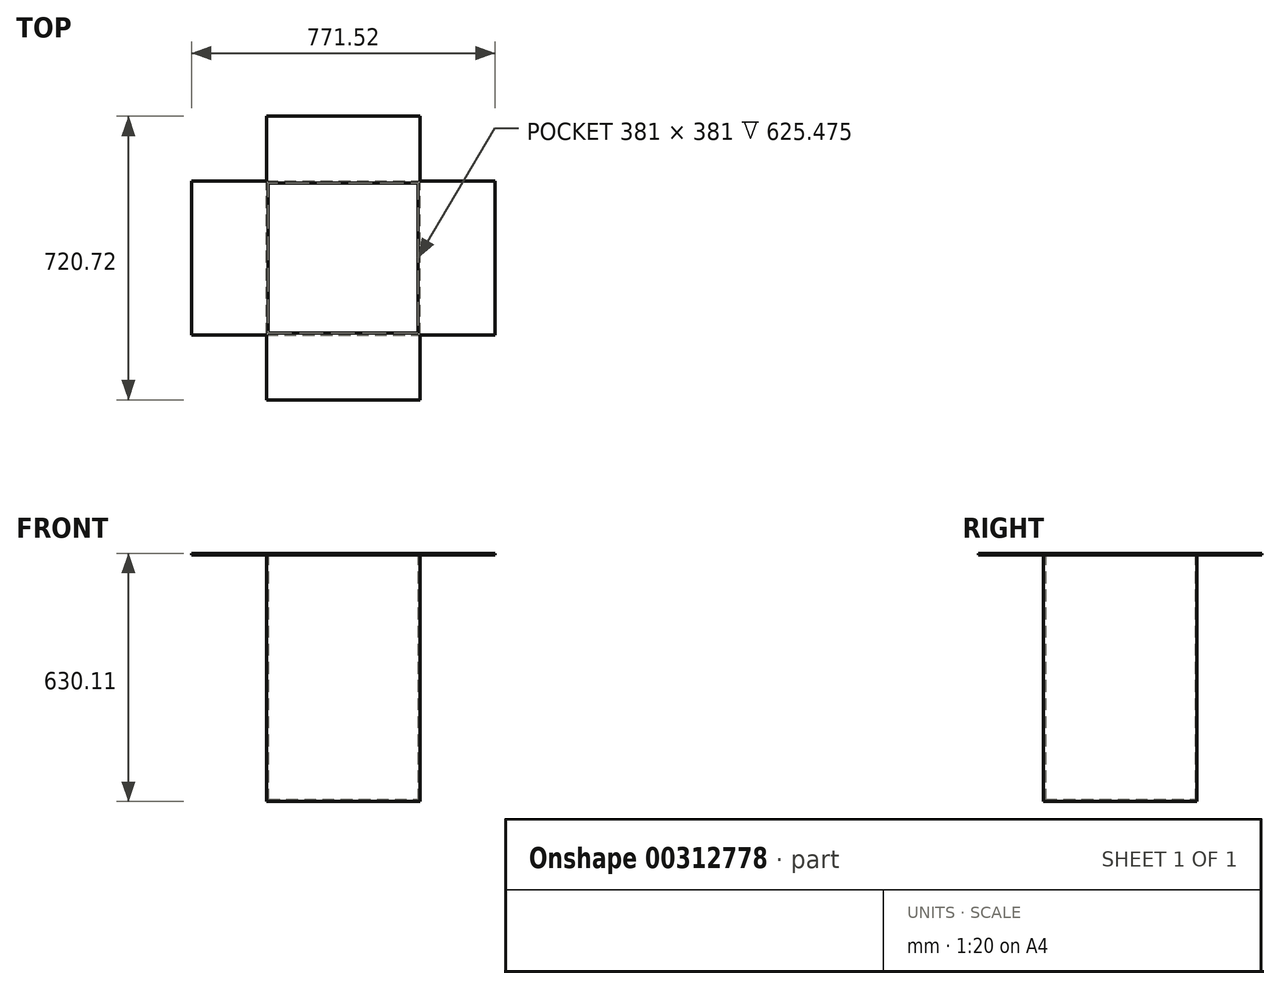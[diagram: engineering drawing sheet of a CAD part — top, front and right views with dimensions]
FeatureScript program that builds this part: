
annotation { "Feature Type Name" : "Feature", "Feature Type Description" : "" }
export const myFeature = defineFeature(function(context is Context, id is Id, definition is map)
    precondition{}
    {
        {
            var Q0;
            Q0=qCreatedBy(makeId("Top.planeOp"),FACE);
            var sketch = newSketch(context, id + "F0", { "sketchPlane" : qUnion([Q0])});
            skLineSegment(sketch, "E0.bottom", {"start": v(0, 0) * mm, "end": v(390.53, 0) * mm});
            skLineSegment(sketch, "E0.top", {"start": v(0, 390.53) * mm, "end": v(390.53, 390.53) * mm});
            skLineSegment(sketch, "E0.left", {"start": v(0, 0) * mm, "end": v(0, 390.53) * mm});
            skLineSegment(sketch, "E0.right", {"start": v(390.53, 0) * mm, "end": v(390.53, 390.53) * mm});
            skLineSegment(sketch, "E1.0", {"start": v(4.76, 4.76) * mm, "end": v(4.76, 385.76) * mm});
            skLineSegment(sketch, "E1.1", {"start": v(4.76, 4.76) * mm, "end": v(385.76, 4.76) * mm});
            skLineSegment(sketch, "E1.2", {"start": v(385.76, 4.76) * mm, "end": v(385.76, 385.76) * mm});
            skLineSegment(sketch, "E1.3", {"start": v(4.76, 385.76) * mm, "end": v(385.76, 385.76) * mm});
            skSolve(sketch);
        }
        {
            var Q0;
            Q0 = qSketchRegion(id + "F0", true);
            extrude(context, id + "F1", {"entities" : qUnion([Q0]), "depth" : 625.47 * mm});
        }
        {
            var Q0;
            Q0=makeQuery(id+"F0.imprint","IMPRINT",FACE,{"disambiguationData":[TD([[makeQuery(id+"F0.imprint","IMPRINT",EDGE,{"derivedFrom":sQuery(id+"F0.wireOp",EDGE,"E1.0")}),-1.0]])]});
            extrude(context, id + "F2", {"entities" : qUnion([Q0]), "operationType" : NewBodyOperationType.ADD, "depth" : 4.64 * mm});
        }
        {
            var Q0;
            Q0=qCreatedBy(makeId("Top.planeOp"),FACE);
            var Q1;
            Q1=makeQuery(id+"F1.opExtrude","CAP_VERTEX",VERTEX,{"disambiguationData":[OSD([sQuery(id+"F0.wireOp",EDGE,"E1.0"),sQuery(id+"F0.wireOp",EDGE,"E1.3")])],"isStart":false});
            cPlane(context, id + "F3", {"entities" : qUnion([Q0, Q1]), "cplaneType" : CPlaneType.PLANE_POINT, "offset" : 25.4 * mm, "width" : 152.4 * mm, "height" : 152.4 * mm});
        }
        {
            var Q0;
            Q0=qCreatedBy(id+"F3.planeOp",FACE);
            var sketch = newSketch(context, id + "F4", { "sketchPlane" : qUnion([Q0])});
            skLineSegment(sketch, "E2", {"start": v(0, 0) * mm, "end": v(-190.5, 0) * mm});
            skLineSegment(sketch, "E3", {"start": v(-190.5, 0) * mm, "end": v(-190.5, 390.53) * mm});
            skLineSegment(sketch, "E4", {"start": v(-190.5, 390.53) * mm, "end": v(0, 390.53) * mm});
            skLineSegment(sketch, "E5.top", {"start": v(0, 555.62) * mm, "end": v(390.53, 555.62) * mm});
            skLineSegment(sketch, "E5.left", {"start": v(0, 390.53) * mm, "end": v(0, 555.62) * mm});
            skLineSegment(sketch, "E5.right", {"start": v(390.53, 390.53) * mm, "end": v(390.53, 555.62) * mm});
            skLineSegment(sketch, "E6.bottom", {"start": v(390.53, 390.53) * mm, "end": v(581.03, 390.53) * mm});
            skLineSegment(sketch, "E6.top", {"start": v(390.53, 0) * mm, "end": v(581.03, 0) * mm});
            skLineSegment(sketch, "E6.right", {"start": v(581.03, 390.53) * mm, "end": v(581.03, 0) * mm});
            skLineSegment(sketch, "E7.top", {"start": v(0, -165.1) * mm, "end": v(390.53, -165.1) * mm});
            skLineSegment(sketch, "E7.left", {"start": v(0, 0) * mm, "end": v(0, -165.1) * mm});
            skLineSegment(sketch, "E7.right", {"start": v(390.53, 0) * mm, "end": v(390.53, -165.1) * mm});
            skLineSegment(sketch, "E8.bottom", {"start": v(4.76, 385.76) * mm, "end": v(385.76, 385.76) * mm});
            skLineSegment(sketch, "E8.top", {"start": v(4.76, 4.76) * mm, "end": v(385.76, 4.76) * mm});
            skLineSegment(sketch, "E8.left", {"start": v(4.76, 385.76) * mm, "end": v(4.76, 4.76) * mm});
            skLineSegment(sketch, "E8.right", {"start": v(385.76, 385.76) * mm, "end": v(385.76, 4.76) * mm});
            skSolve(sketch);
        }
        {
            var Q0;
            Q0=makeQuery(id+"F4.imprint","IMPRINT",FACE,{"disambiguationData":[TD([[makeQuery(id+"F4.imprint","IMPRINT",EDGE,{"derivedFrom":sQuery(id+"F4.wireOp",EDGE,"E2")}),-1.0]])]});
            extrude(context, id + "F5", {"entities" : qUnion([Q0]), "operationType" : NewBodyOperationType.ADD, "depth" : 4.64 * mm});
        }
    });
